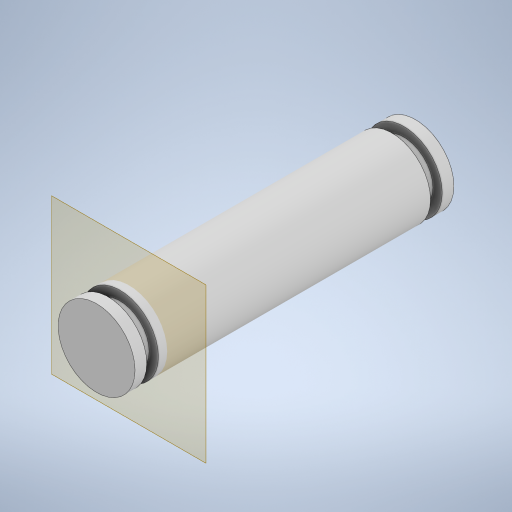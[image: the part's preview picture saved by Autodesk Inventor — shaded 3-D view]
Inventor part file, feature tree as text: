
AUTODESK INVENTOR PART (.ipt)
format: ipt  version: 2024 (Build 280153000, 153)  size: 619,008 bytes
history: native  units: mm
features: sketch x5, extrude x5, plane x3, other x3, direct_edit x1, move_body x1
ambient origin geometry x8: Origin, YZ Plane, XZ Plane, XY Plane, X Axis, Y Axis, Z Axis, Center Point
bodies: Solid1 (feature_tree)
feature tree (18):
  plane  "Work Plane1"
  sketch  "Sketch1"  dims[d0=0.35mm d1=90.0mm d2=0.0mm]
  plane  "Work Plane2"
  plane  "Work Plane3"
  extrude  "Extrusion1"  Depth=90.0mm TaperAngle=0.0deg
  direct_edit  "Direct Edit1"
  extrude  "Extrusion4"  Depth=3.0mm
  extrude  "Extrusion5"  Depth=4.0mm TaperAngle=0.0deg
  extrude  "Extrusion6"  Depth=27.0mm
  extrude  "Extrusion7"  Depth=4.0mm
  sketch  "Sketch5"  dims[d8=0.0mm d9=0.0mm d10=3.0mm d11=20.0mm]
  sketch  "Sketch6"  dims[d12=4.0mm d13=0.0mm d14=4.0mm d15=0.0mm]
  sketch  "Sketch7"  dims[d16=9.4mm d17=27.0mm]
  sketch  "Sketch8"  dims[d18=14.54197mm d19=14.54197mm d20=26.870058mm d21=19.0mm d22=26.870058mm d23=35.107422mm d24=38.0mm d25=26.870058mm d26=14.54197mm d27=19.0mm d28=35.107422mm d29=26.870058mm d30=35.107422mm d31=38.0mm d32=26.870058mm d35=20.0mm d36=4.0mm d37=0.0mm d38=4.0mm d39=0.0mm]
  move_body  "Move1"
  other  "<userpath>\Documents\Inventor\robot arm\arms\arms.iam"
  other  "arms.iam"
  other  "upper arm pulley:1"
